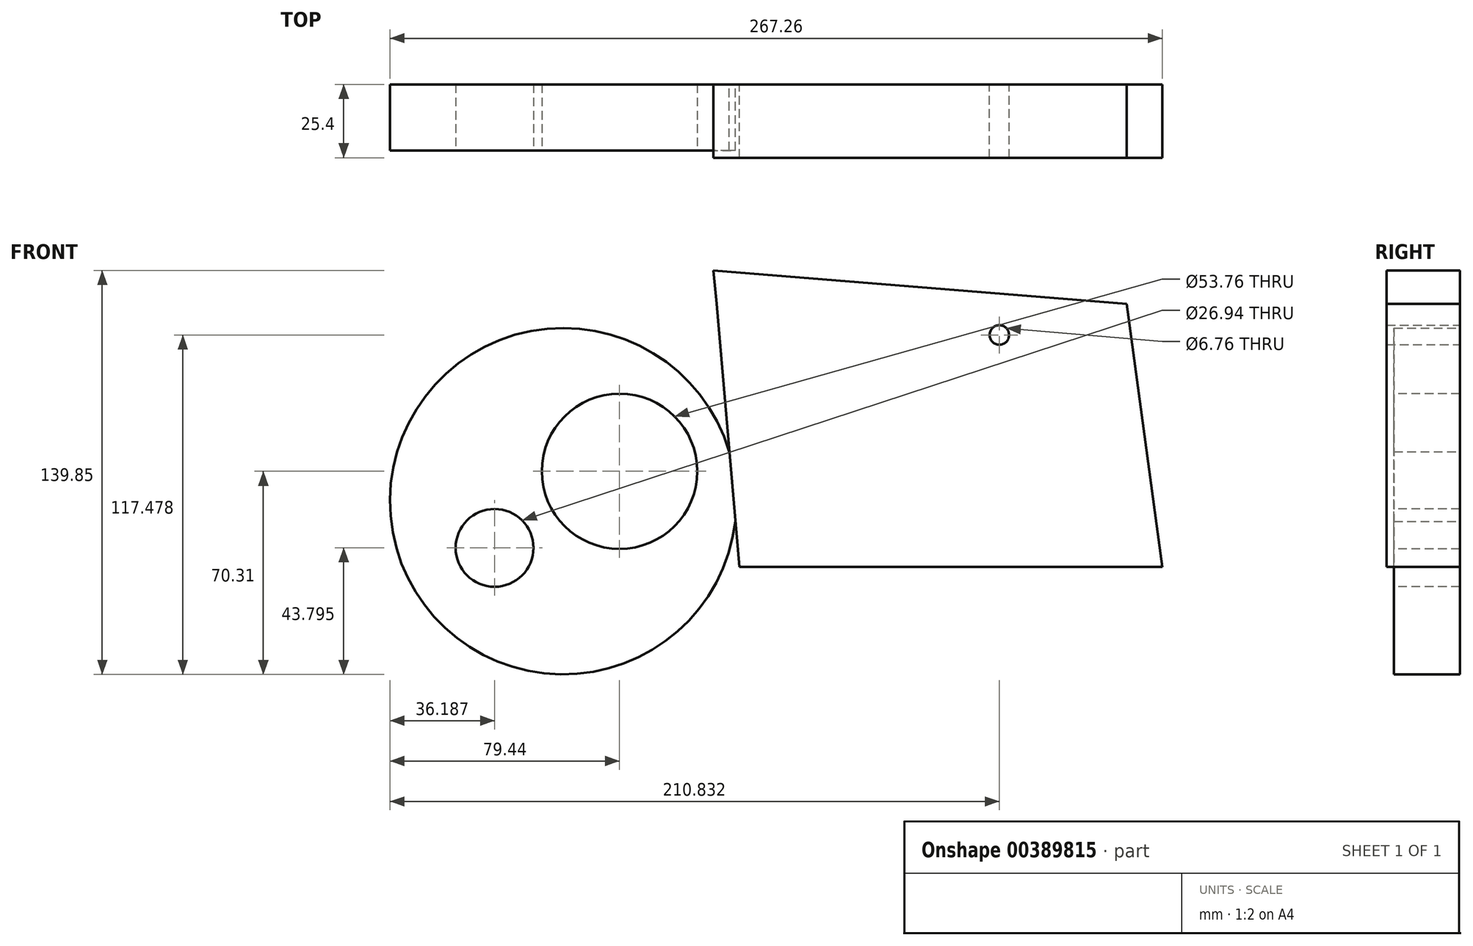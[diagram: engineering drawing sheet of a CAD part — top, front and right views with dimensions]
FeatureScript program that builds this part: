
annotation { "Feature Type Name" : "Feature", "Feature Type Description" : "" }
export const myFeature = defineFeature(function(context is Context, id is Id, definition is map)
    precondition{}
    {
        {
            var Q0;
            Q0=qCreatedBy(makeId("Front.planeOp"),FACE);
            var sketch = newSketch(context, id + "F0", { "sketchPlane" : qUnion([Q0])});
            skCircle(sketch, "E0", {"center": v(-19.49, -10.35) * mm, "radius": 59.95 * mm});
            skSolve(sketch);
        }
        {
            var Q0;
            Q0=makeQuery(id+"F0.imprint","IMPRINT",FACE,{"disambiguationData":[TD([[makeQuery(id+"F0.imprint","IMPRINT",EDGE,{"derivedFrom":sQuery(id+"F0.wireOp",EDGE,"E0")}),1.0]])]});
            extrude(context, id + "F1", {"entities" : qUnion([Q0]), "depth" : 22.86 * mm});
        }
        {
            var Q0;
            Q0=makeQuery(id+"F1.opExtrude","CAP_FACE",FACE,{"disambiguationData":[OSD([sQuery(id+"F0.wireOp",EDGE,"E0")])],"isStart":false});
            var sketch = newSketch(context, id + "F2", { "sketchPlane" : qUnion([Q0])});
            skCircle(sketch, "E1", {"center": v(0, 0) * mm, "radius": 26.88 * mm});
            skSolve(sketch);
        }
        {
            var Q0;
            Q0=makeQuery(id+"F2.imprint","IMPRINT",FACE,{"disambiguationData":[TD([[makeQuery(id+"F2.imprint","IMPRINT",EDGE,{"derivedFrom":sQuery(id+"F2.wireOp",EDGE,"E1")}),1.0]])]});
            extrude(context, id + "F3", {"entities" : qUnion([Q0]), "operationType" : NewBodyOperationType.REMOVE, "endBound" : BoundingType.THROUGH_ALL, "oppositeDirection" : true, "depth" : 25.4 * mm});
        }
        {
            var Q0;
            Q0=makeQuery(id+"F1.opExtrude","CAP_FACE",FACE,{"disambiguationData":[OSD([sQuery(id+"F0.wireOp",EDGE,"E0")])],"isStart":false});
            var sketch = newSketch(context, id + "F4", { "sketchPlane" : qUnion([Q0])});
            skCircle(sketch, "E2", {"center": v(-43.25, -26.52) * mm, "radius": 13.47 * mm});
            skSolve(sketch);
        }
        {
            var Q0;
            Q0=makeQuery(id+"F4.imprint","IMPRINT",FACE,{"disambiguationData":[TD([[makeQuery(id+"F4.imprint","IMPRINT",EDGE,{"derivedFrom":sQuery(id+"F4.wireOp",EDGE,"E2")}),1.0]])]});
            extrude(context, id + "F5", {"entities" : qUnion([Q0]), "operationType" : NewBodyOperationType.REMOVE, "endBound" : BoundingType.THROUGH_ALL, "oppositeDirection" : true, "depth" : 25.4 * mm});
        }
        {
            var Q0;
            Q0=qCreatedBy(makeId("Front.planeOp"),FACE);
            var sketch = newSketch(context, id + "F6", { "sketchPlane" : qUnion([Q0])});
            skLineSegment(sketch, "E3", {"start": v(32.5, 69.54) * mm, "end": v(33.55, 57.95) * mm});
            skLineSegment(sketch, "E4", {"start": v(33.55, 57.95) * mm, "end": v(41.41, -33.06) * mm});
            skLineSegment(sketch, "E5", {"start": v(41.41, -33.06) * mm, "end": v(187.82, -33.06) * mm});
            skLineSegment(sketch, "E6", {"start": v(187.82, -33.06) * mm, "end": v(175.4, 57.95) * mm});
            skLineSegment(sketch, "E7", {"start": v(175.4, 57.95) * mm, "end": v(32.5, 69.54) * mm});
            skLineSegment(sketch, "E8", {"start": v(175.4, 57.95) * mm, "end": v(173.8, 69.54) * mm});
            skLineSegment(sketch, "E9", {"start": v(173.8, 69.54) * mm, "end": v(32.5, 69.54) * mm});
            skCircle(sketch, "E10", {"center": v(131.4, 47.17) * mm, "radius": 16.06 * mm});
            skSolve(sketch);
        }
        {
            var Q0;
            {var subQ1=sQuery(id+"F6.wireOp",EDGE,"E3");Q0=makeQuery(id+"F6.imprint","IMPRINT",FACE,{"disambiguationData":[TD([[makeQuery(id+"F6.imprint","IMPRINT",EDGE,{"derivedFrom":subQ1}),1.0]])]});}
            var Q1;
            {var subQ0=sQuery(id+"F6.wireOp",EDGE,"E10");var subQ1=sQuery(id+"F6.wireOp",EDGE,"E7");var subQ2=makeQuery(id+"F6.imprint","INTERSECT",VERTEX,{"disambiguationData":[OD(0.0)],"derivedFrom":[subQ1,subQ0]});Q1=makeQuery(id+"F6.imprint","IMPRINT",FACE,{"disambiguationData":[TD([[makeQuery(id+"F6.imprint","IMPRINT",EDGE,{"disambiguationData":[TD([[subQ2,-1.0]])],"derivedFrom":subQ1}),1.0]])]});}
            extrude(context, id + "F7", {"entities" : qUnion([Q0, Q1]), "operationType" : NewBodyOperationType.ADD, "depth" : 25.4 * mm});
        }
        {
            var Q0;
            Q0=sQuery(id+"F6.wireOp",VERTEX,"E10.center");
            var Q1;
            Q1=makeQuery(id+"F1.opExtrude","SWEPT_BODY",BODY,{"disambiguationData":[OSD([sQuery(id+"F0.wireOp",EDGE,"E0")])]});
            hole(context, id + "F8", {"style" : HoleStyle.SIMPLE, "endStyle" : HoleEndStyle.THROUGH, "oppositeDirection" : true, "holeDiameter" : 6.76 * mm, "isTappedThrough" : true, "tappedDepth" : 12.7 * mm, "tapClearance" : 3, "locations" : qUnion([Q0]), "scope" : qUnion([Q1])});
        }
    });
